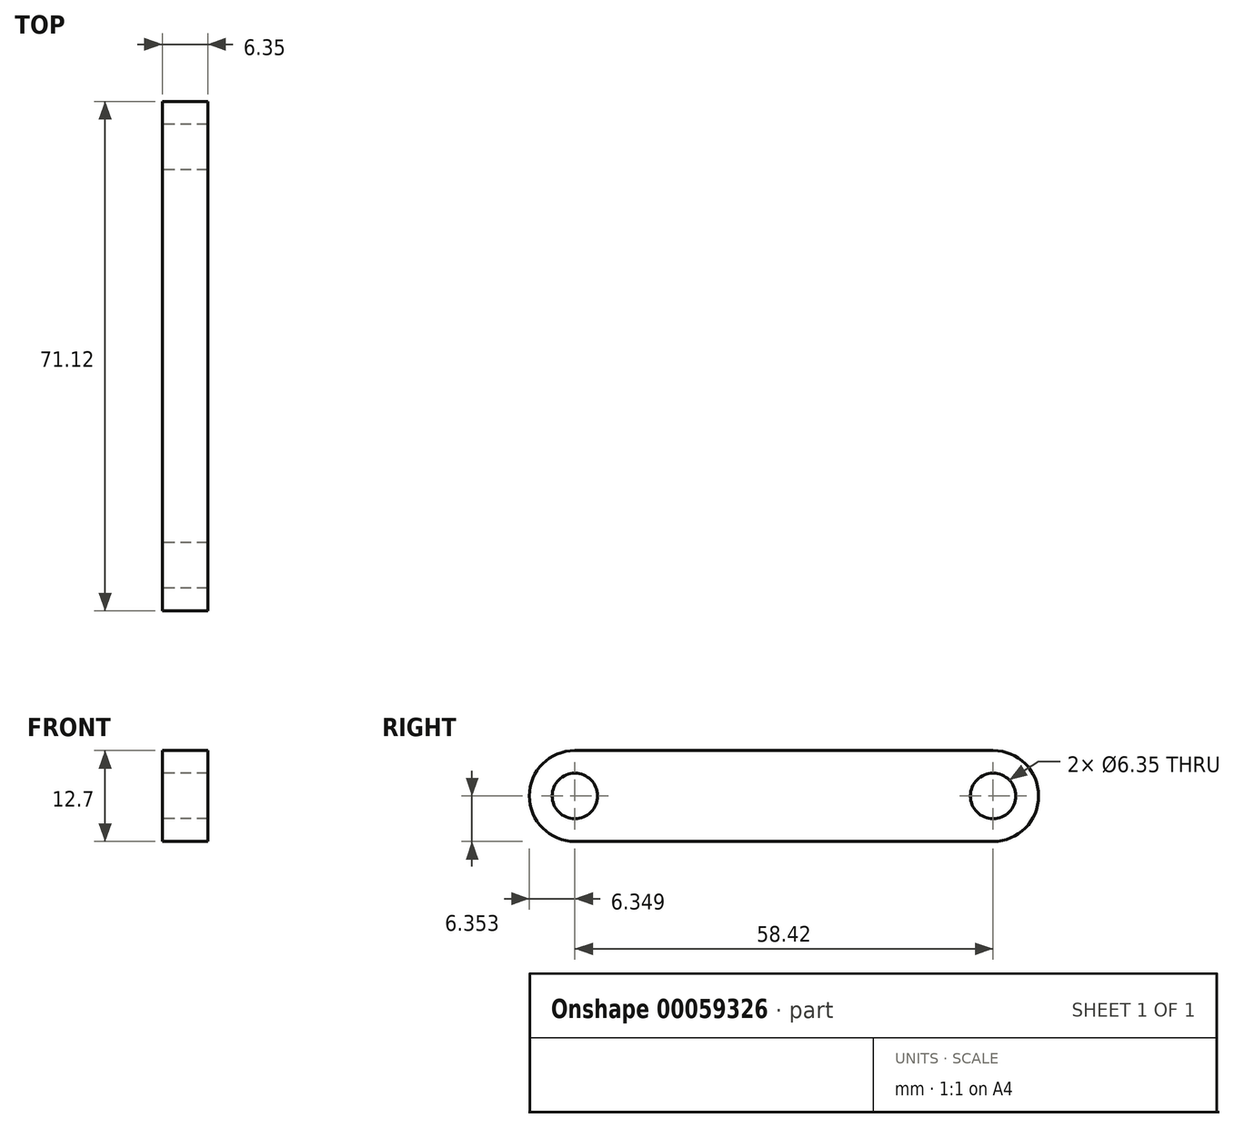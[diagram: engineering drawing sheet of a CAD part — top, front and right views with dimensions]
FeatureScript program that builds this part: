
annotation { "Feature Type Name" : "Feature", "Feature Type Description" : "" }
export const myFeature = defineFeature(function(context is Context, id is Id, definition is map)
    precondition{}
    {
        {
            var Q0;
            Q0=qCreatedBy(makeId("Right.planeOp"),FACE);
            var sketch = newSketch(context, id + "F0", { "sketchPlane" : qUnion([Q0])});
            skLineSegment(sketch, "E0.bottom", {"start": v(-27.5, 6.66) * mm, "end": v(30.93, 6.66) * mm});
            skLineSegment(sketch, "E0.top", {"start": v(-27.5, -6.04) * mm, "end": v(30.93, -6.04) * mm});
            skArc(sketch, "E1", {"start": v(-27.5, 6.66) * mm, "mid": v(-33.84, 0.31) * mm, "end": v(-27.5, -6.04) * mm});
            skArc(sketch, "E2", {"start": v(30.93, -6.04) * mm, "mid": v(37.28, 0.31) * mm, "end": v(30.93, 6.66) * mm});
            skCircle(sketch, "E3", {"center": v(-27.5, 0.31) * mm, "radius": 3.18 * mm});
            skCircle(sketch, "E4", {"center": v(30.93, 0.31) * mm, "radius": 3.18 * mm});
            skSolve(sketch);
        }
        {
            var Q0;
            Q0 = qSketchRegion(id + "F0", true);
            extrude(context, id + "F1", {"entities" : qUnion([Q0]), "depth" : 6.35 * mm});
        }
    });
